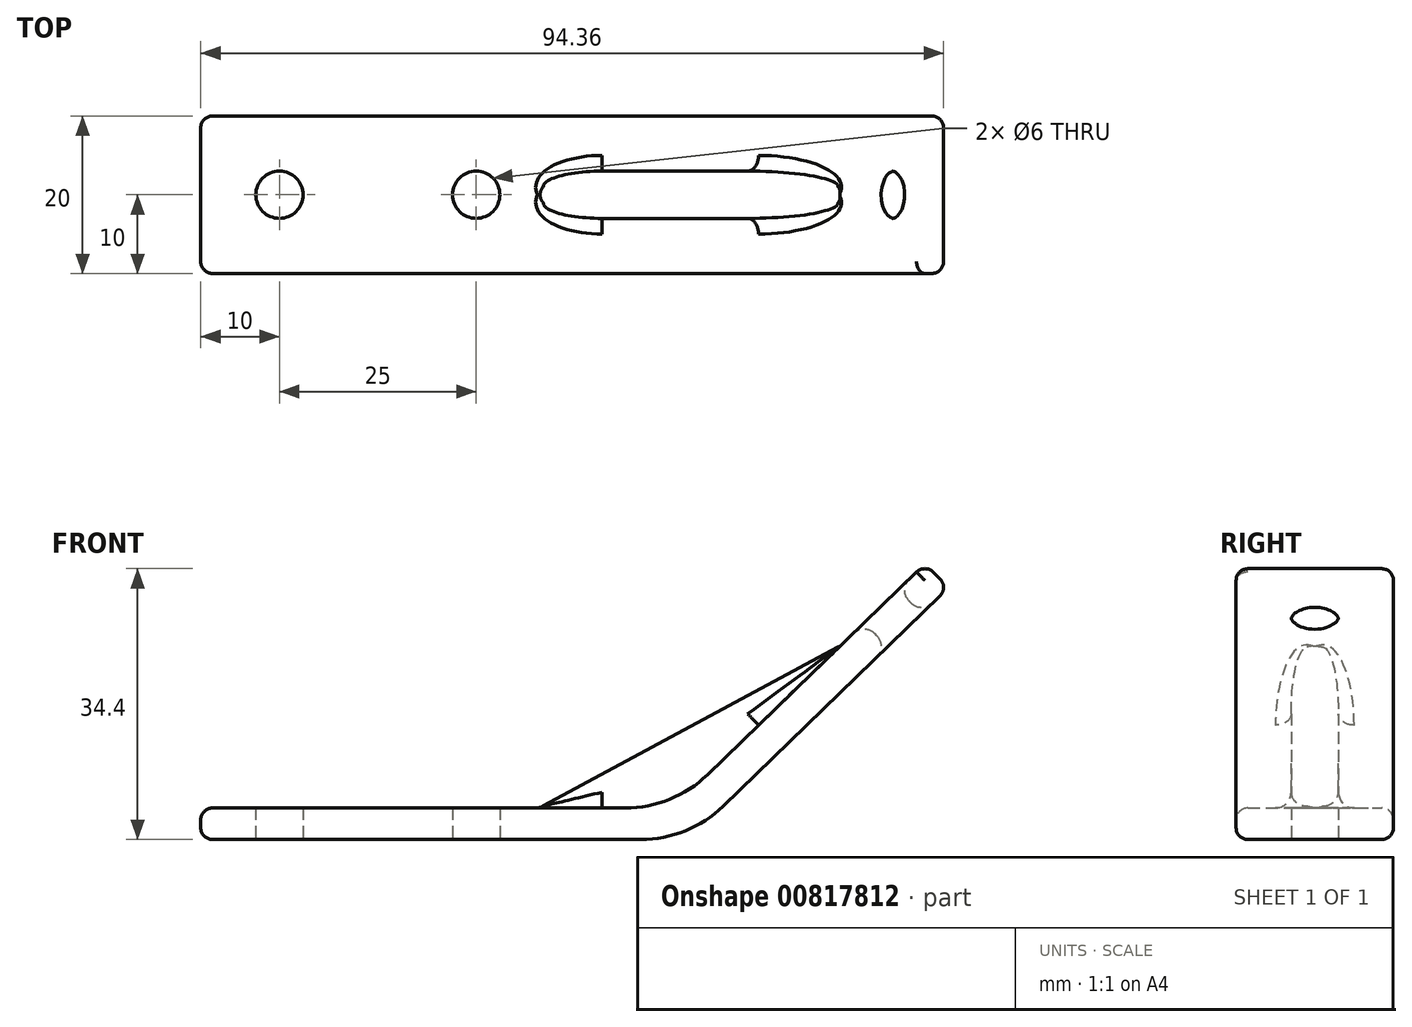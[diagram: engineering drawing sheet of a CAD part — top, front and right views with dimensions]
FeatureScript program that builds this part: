
annotation { "Feature Type Name" : "Feature", "Feature Type Description" : "" }
export const myFeature = defineFeature(function(context is Context, id is Id, definition is map)
    precondition{}
    {
        {
            var Q0;
            Q0=qCreatedBy(makeId("Top.planeOp"),FACE);
            var sketch = newSketch(context, id + "F0", { "sketchPlane" : qUnion([Q0])});
            skLineSegment(sketch, "E0.bottom", {"start": v(30, -10) * mm, "end": v(-30, -10) * mm});
            skLineSegment(sketch, "E0.top", {"start": v(30, 10) * mm, "end": v(-30, 10) * mm});
            skLineSegment(sketch, "E0.left", {"start": v(30, -10) * mm, "end": v(30, 10) * mm});
            skLineSegment(sketch, "E0.right", {"start": v(-30, -10) * mm, "end": v(-30, 10) * mm});
            skPoint(sketch, "E0.middle", {"position": v(0, 0) * mm});
            skLineSegment(sketch, "E1", {"start": v(-30, 0) * mm, "end": v(-20, 0) * mm, "construction": true});
            skLineSegment(sketch, "E2", {"start": v(-20, 0) * mm, "end": v(-5, 0) * mm, "construction": true});
            skLineSegment(sketch, "E3", {"start": v(-5, 0) * mm, "end": v(5, 0) * mm, "construction": true});
            skCircle(sketch, "E4", {"center": v(-20, 0) * mm, "radius": 3 * mm});
            skCircle(sketch, "E5", {"center": v(5, 0) * mm, "radius": 3 * mm});
            skSolve(sketch);
        }
        {
            var Q0;
            Q0=makeQuery(id+"F0.imprint","IMPRINT",FACE,{"disambiguationData":[TD([[makeQuery(id+"F0.imprint","IMPRINT",EDGE,{"derivedFrom":sQuery(id+"F0.wireOp",EDGE,"E0.bottom")}),-1.0]])]});
            extrude(context, id + "F1", {"entities" : qUnion([Q0]), "depth" : 4 * mm, "offsetDistance" : 25 * mm});
        }
        {
            var Q0;
            Q0=makeQuery(id+"F1.opExtrude","SWEPT_FACE",FACE,{"disambiguationData":[OSD([sQuery(id+"F0.wireOp",EDGE,"E0.bottom")])]});
            var sketch = newSketch(context, id + "F2", { "sketchPlane" : qUnion([Q0])});
            skLineSegment(sketch, "E6.bottom", {"start": v(30, 0) * mm, "end": v(65, 0) * mm});
            skLineSegment(sketch, "E6.top", {"start": v(30, 35) * mm, "end": v(65, 35) * mm});
            skLineSegment(sketch, "E6.left", {"start": v(30, 0) * mm, "end": v(30, 35) * mm, "construction": true});
            skLineSegment(sketch, "E6.right", {"start": v(65, 0) * mm, "end": v(65, 35) * mm, "construction": true});
            skLineSegment(sketch, "E7", {"start": v(65, 35) * mm, "end": v(65, 32) * mm, "construction": true});
            skLineSegment(sketch, "E8", {"start": v(65, 35) * mm, "end": v(62, 35) * mm, "construction": true});
            skLineSegment(sketch, "E9", {"start": v(30, 4) * mm, "end": v(62, 35) * mm});
            skLineSegment(sketch, "E10", {"start": v(65, 32) * mm, "end": v(62, 35) * mm});
            skLineSegment(sketch, "E11", {"start": v(30, 0) * mm, "end": v(32, 0) * mm, "construction": true});
            skLineSegment(sketch, "E12", {"start": v(65, 32) * mm, "end": v(32, 0) * mm});
            skSolve(sketch);
        }
        {
            var Q0;
            Q0=makeQuery(id+"F2.imprint","IMPRINT",FACE,{"disambiguationData":[TD([[makeQuery(id+"F2.imprint","IMPRINT",EDGE,{"derivedFrom":sQuery(id+"F2.wireOp",EDGE,"E9")}),-1.0]])]});
            extrude(context, id + "F3", {"entities" : qUnion([Q0]), "operationType" : NewBodyOperationType.ADD, "oppositeDirection" : true, "depth" : 20 * mm, "offsetDistance" : 25 * mm});
        }
        {
            var Q0;
            {var subQ0=sQuery(id+"F0.wireOp",EDGE,"E0.left");Q0=makeQuery(id+"F3.boolean.opBoolean","MERGE",EDGE,{"derivedFrom":[makeQuery(id+"F1.opExtrude","CAP_EDGE",EDGE,{"disambiguationData":[OSD([subQ0])],"isStart":false}),makeQuery(id+"F3.opExtrude","SWEPT_EDGE",EDGE,{"disambiguationData":[OSD([sQuery(id+"F0.wireOp",EDGE,"E0.bottom"),subQ0,sQuery(id+"F2.wireOp",EDGE,"E9")])]})]});}
            var Q1;
            Q1=makeQuery(id+"F3.opExtrude","SWEPT_EDGE",EDGE,{"disambiguationData":[OSD([sQuery(id+"F2.wireOp",EDGE,"E6.bottom"),sQuery(id+"F2.wireOp",EDGE,"E12")])]});
            fillet(context, id + "F4", {"entities" : qUnion([Q0, Q1]), "radius" : 15 * mm, "tangentPropagation" : true, "allowEdgeOverflow" : false});
        }
        {
            var Q0;
            Q0=qCreatedBy(makeId("Front.planeOp"),FACE);
            var sketch = newSketch(context, id + "F5", { "sketchPlane" : qUnion([Q0])});
            skLineSegment(sketch, "E13", {"start": v(11.51, 0.58) * mm, "end": v(25.37, 1.73) * mm});
            skLineSegment(sketch, "E14", {"start": v(25.37, 1.73) * mm, "end": v(31.95, 3.64) * mm});
            skLineSegment(sketch, "E15", {"start": v(31.95, 3.64) * mm, "end": v(41.28, 12.04) * mm});
            skLineSegment(sketch, "E16", {"start": v(41.28, 12.04) * mm, "end": v(55.4, 25.04) * mm});
            skLineSegment(sketch, "E17", {"start": v(55.4, 25.04) * mm, "end": v(54.3, 26.22) * mm});
            skLineSegment(sketch, "E18", {"start": v(54.3, 26.22) * mm, "end": v(10.65, 2.7) * mm});
            skLineSegment(sketch, "E19", {"start": v(10.65, 2.7) * mm, "end": v(11.51, 0.58) * mm});
            skSolve(sketch);
        }
        {
            var Q0;
            Q0=makeQuery(id+"F5.imprint","IMPRINT",FACE,{"disambiguationData":[TD([[makeQuery(id+"F5.imprint","IMPRINT",EDGE,{"derivedFrom":sQuery(id+"F5.wireOp",EDGE,"E13")}),1.0]])]});
            extrude(context, id + "F6", {"entities" : qUnion([Q0]), "operationType" : NewBodyOperationType.ADD, "endBound" : BoundingType.SYMMETRIC, "depth" : 6 * mm, "offsetDistance" : 25 * mm});
        }
        {
            var Q0;
            Q0=makeQuery(id+"F1.opExtrude","SWEPT_FACE",FACE,{"disambiguationData":[OSD([sQuery(id+"F0.wireOp",EDGE,"E0.right")])]});
            var Q1;
            Q1=makeQuery(id+"F3.boolean.opBoolean","MERGE",FACE,{"derivedFrom":[makeQuery(id+"F1.opExtrude","SWEPT_FACE",FACE,{"disambiguationData":[OSD([sQuery(id+"F0.wireOp",EDGE,"E0.top")])]}),makeQuery(id+"F3.opExtrude","CAP_FACE",FACE,{"disambiguationData":[OSD([sQuery(id+"F0.wireOp",EDGE,"E0.bottom"),sQuery(id+"F0.wireOp",EDGE,"E0.left"),sQuery(id+"F2.wireOp",EDGE,"E6.bottom"),sQuery(id+"F2.wireOp",EDGE,"E9"),sQuery(id+"F2.wireOp",EDGE,"E10"),sQuery(id+"F2.wireOp",EDGE,"E12")])],"isStart":false})]});
            var Q2;
            {var subQ0=sQuery(id+"F0.wireOp",EDGE,"E0.bottom");Q2=makeQuery(id+"F3.boolean.opBoolean","MERGE",FACE,{"derivedFrom":[makeQuery(id+"F1.opExtrude","SWEPT_FACE",FACE,{"disambiguationData":[OSD([subQ0])]}),makeQuery(id+"F3.opExtrude","CAP_FACE",FACE,{"disambiguationData":[OSD([subQ0,sQuery(id+"F0.wireOp",EDGE,"E0.left"),sQuery(id+"F2.wireOp",EDGE,"E6.bottom"),sQuery(id+"F2.wireOp",EDGE,"E9"),sQuery(id+"F2.wireOp",EDGE,"E10"),sQuery(id+"F2.wireOp",EDGE,"E12")])],"isStart":true})]});}
            var Q3;
            Q3=makeQuery(id+"F3.opExtrude","SWEPT_FACE",FACE,{"disambiguationData":[OSD([sQuery(id+"F2.wireOp",EDGE,"E10")])]});
            fillet(context, id + "F7", {"entities" : qUnion([Q0, Q1, Q2, Q3]), "radius" : 1.5 * mm, "tangentPropagation" : true, "allowEdgeOverflow" : false});
        }
        {
            var Q0;
            Q0=makeQuery(id+"F6.boolean.opBoolean","INTERSECT",EDGE,{"derivedFrom":[makeQuery(id+"F1.opExtrude","CAP_FACE",FACE,{"disambiguationData":[OSD([sQuery(id+"F0.wireOp",EDGE,"E0.bottom"),sQuery(id+"F0.wireOp",EDGE,"E0.top"),sQuery(id+"F0.wireOp",EDGE,"E0.left"),sQuery(id+"F0.wireOp",EDGE,"E0.right"),sQuery(id+"F0.wireOp",EDGE,"E4"),sQuery(id+"F0.wireOp",EDGE,"E5")])],"isStart":false}),makeQuery(id+"F6.opExtrude","CAP_FACE",FACE,{"disambiguationData":[OSD([sQuery(id+"F5.wireOp",EDGE,"E13"),sQuery(id+"F5.wireOp",EDGE,"E14"),sQuery(id+"F5.wireOp",EDGE,"E15"),sQuery(id+"F5.wireOp",EDGE,"E16"),sQuery(id+"F5.wireOp",EDGE,"E17"),sQuery(id+"F5.wireOp",EDGE,"E18"),sQuery(id+"F5.wireOp",EDGE,"E19")])],"isStart":false})]});
            var Q1;
            Q1=makeQuery(id+"F6.boolean.opBoolean","INTERSECT",EDGE,{"derivedFrom":[makeQuery(id+"F3.opExtrude","SWEPT_FACE",FACE,{"disambiguationData":[OSD([sQuery(id+"F2.wireOp",EDGE,"E9")])]}),makeQuery(id+"F6.opExtrude","CAP_FACE",FACE,{"disambiguationData":[OSD([sQuery(id+"F5.wireOp",EDGE,"E13"),sQuery(id+"F5.wireOp",EDGE,"E14"),sQuery(id+"F5.wireOp",EDGE,"E15"),sQuery(id+"F5.wireOp",EDGE,"E16"),sQuery(id+"F5.wireOp",EDGE,"E17"),sQuery(id+"F5.wireOp",EDGE,"E18"),sQuery(id+"F5.wireOp",EDGE,"E19")])],"isStart":true})]});
            var Q2;
            Q2=makeQuery(id+"F6.opExtrude","CAP_EDGE",EDGE,{"disambiguationData":[OSD([sQuery(id+"F5.wireOp",EDGE,"E18")])],"isStart":true});
            var Q3;
            Q3=makeQuery(id+"F6.opExtrude","CAP_EDGE",EDGE,{"disambiguationData":[OSD([sQuery(id+"F5.wireOp",EDGE,"E18")])],"isStart":false});
            fillet(context, id + "F8", {"entities" : qUnion([Q0, Q1, Q2, Q3]), "radius" : 2 * mm, "tangentPropagation" : true, "allowEdgeOverflow" : false});
        }
        {
            var Q0;
            Q0=makeQuery(id+"F3.opExtrude","SWEPT_FACE",FACE,{"disambiguationData":[OSD([sQuery(id+"F2.wireOp",EDGE,"E9")])]});
            var sketch = newSketch(context, id + "F9", { "sketchPlane" : qUnion([Q0])});
            skLineSegment(sketch, "E20", {"start": v(54.16, 0) * mm, "end": v(61.16, 0) * mm});
            skCircle(sketch, "E21", {"center": v(61.16, 0) * mm, "radius": 3 * mm});
            skSolve(sketch);
        }
        {
            var Q0;
            Q0=makeQuery(id+"F9.imprint","IMPRINT",FACE,{"disambiguationData":[TD([[makeQuery(id+"F9.imprint","IMPRINT",EDGE,{"derivedFrom":sQuery(id+"F9.wireOp",EDGE,"E21")}),1.0]])]});
            extrude(context, id + "F10", {"entities" : qUnion([Q0]), "operationType" : NewBodyOperationType.REMOVE, "oppositeDirection" : true, "depth" : 5 * mm, "offsetDistance" : 25 * mm});
        }
        {
            var Q0;
            Q0=makeQuery(id+"F10.boolean.opBoolean","COPY",FACE,{"derivedFrom":makeQuery(id+"F10.opExtrude","SWEPT_FACE",FACE,{"disambiguationData":[OSD([sQuery(id+"F9.wireOp",EDGE,"E21")])]})});
            fillet(context, id + "F11", {"entities" : qUnion([Q0]), "radius" : 2 * mm, "tangentPropagation" : true, "allowEdgeOverflow" : false});
        }
    });
